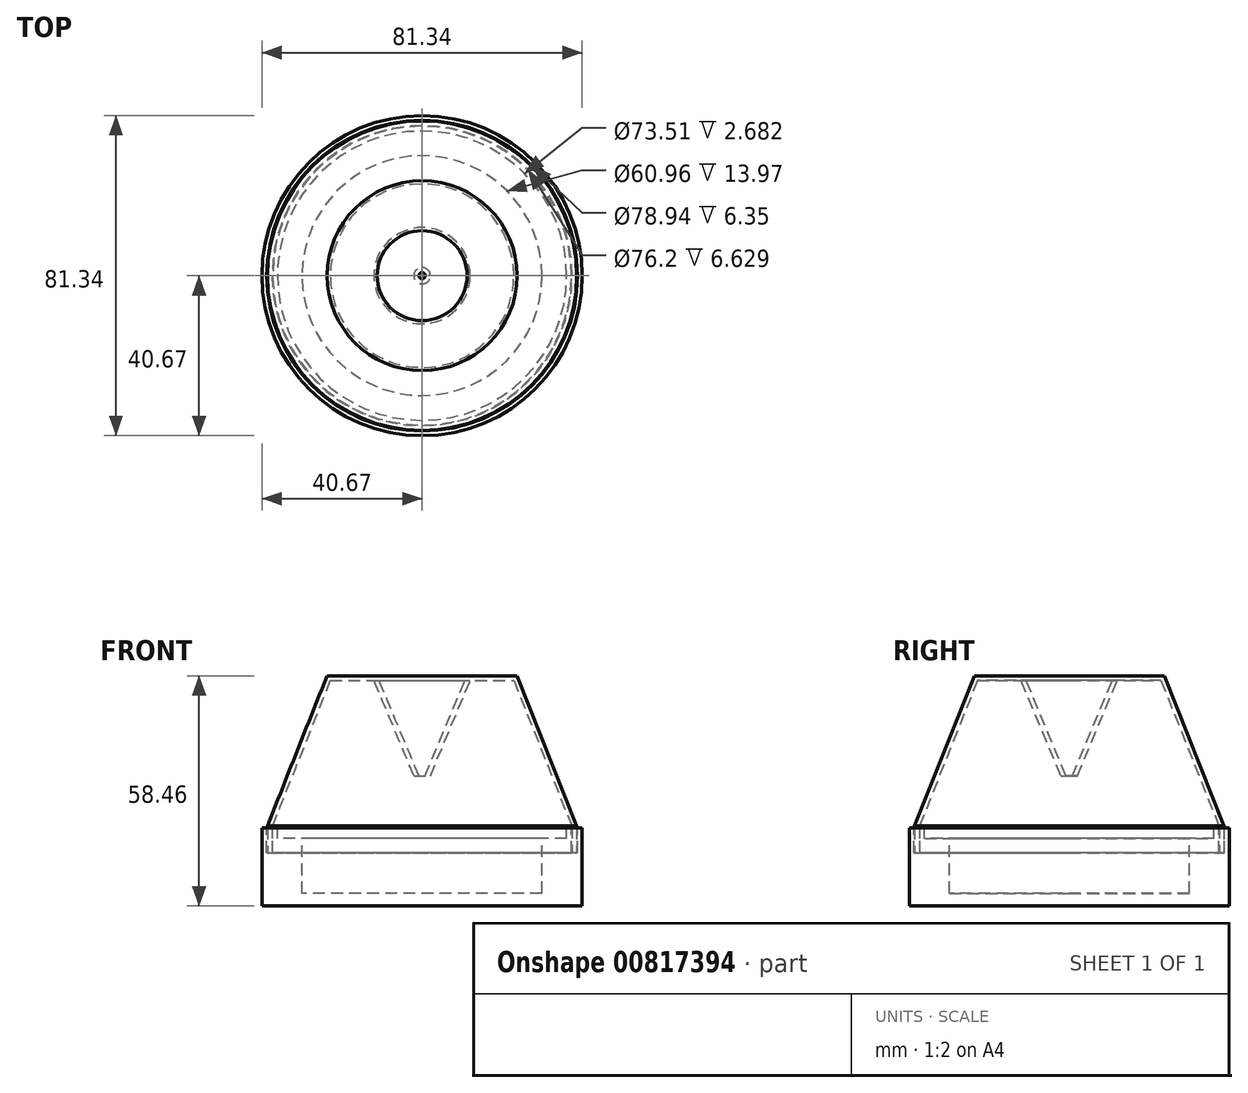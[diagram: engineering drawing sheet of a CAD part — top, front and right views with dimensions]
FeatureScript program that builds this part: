
annotation { "Feature Type Name" : "Feature", "Feature Type Description" : "" }
export const myFeature = defineFeature(function(context is Context, id is Id, definition is map)
    precondition{}
    {
        {
            var Q0;
            Q0=qCreatedBy(makeId("Front.planeOp"),FACE);
            var sketch = newSketch(context, id + "F0", { "sketchPlane" : qUnion([Q0])});
            skLineSegment(sketch, "E0", {"start": v(39.3, 0) * mm, "end": v(24.13, 38.1) * mm});
            skLineSegment(sketch, "E1", {"start": v(24.13, 38.1) * mm, "end": v(11.43, 38.1) * mm});
            skLineSegment(sketch, "E2", {"start": v(11.43, 38.1) * mm, "end": v(0.8, 12.7) * mm});
            skLineSegment(sketch, "E3", {"start": v(39.3, 0) * mm, "end": v(39.3, -6.86) * mm});
            skLineSegment(sketch, "E4.0", {"start": v(12.22, 36.9) * mm, "end": v(2.09, 12.7) * mm});
            skLineSegment(sketch, "E4.1", {"start": v(23.32, 36.9) * mm, "end": v(12.22, 36.9) * mm});
            skLineSegment(sketch, "E4.2", {"start": v(38.1, -0.23) * mm, "end": v(23.32, 36.9) * mm});
            skLineSegment(sketch, "E4.3", {"start": v(38.1, -0.23) * mm, "end": v(38.1, -6.86) * mm});
            skLineSegment(sketch, "E5", {"start": v(38.1, -6.86) * mm, "end": v(39.3, -6.86) * mm});
            skLineSegment(sketch, "E6", {"start": v(0.8, 12.7) * mm, "end": v(2.09, 12.7) * mm});
            skSolve(sketch);
        }
        {
            var Q0;
            Q0=qCreatedBy(makeId("Front.planeOp"),FACE);
            var sketch = newSketch(context, id + "F1", { "sketchPlane" : qUnion([Q0])});
            skLineSegment(sketch, "E7", {"start": v(0, 0) * mm, "end": v(0, 61.65) * mm});
            skSolve(sketch);
        }
        {
            var Q0;
            Q0=makeQuery(id+"F0.imprint","IMPRINT",FACE,{"disambiguationData":[TD([[makeQuery(id+"F0.imprint","IMPRINT",EDGE,{"derivedFrom":sQuery(id+"F0.wireOp",EDGE,"E0")}),1.0]])]});
            var Q1;
            Q1=sQuery(id+"F1.wireOp",EDGE,"E7");
            revolve(context, id + "F2", {"surfaceOperationType" : NewSurfaceOperationType.NEW, "entities" : qUnion([Q0]), "axis" : qUnion([Q1]), "revolveType" : RevolveType.FULL});
        }
        {
            var Q0;
            Q0=qCreatedBy(makeId("Front.planeOp"),FACE);
            var sketch = newSketch(context, id + "F3", { "sketchPlane" : qUnion([Q0])});
            skLineSegment(sketch, "E8", {"start": v(40.67, -0.5) * mm, "end": v(40.67, -20.36) * mm});
            skLineSegment(sketch, "E9", {"start": v(40.67, -20.36) * mm, "end": v(0, -20.36) * mm});
            skLineSegment(sketch, "E10", {"start": v(0, -20.36) * mm, "end": v(0, -17.16) * mm});
            skLineSegment(sketch, "E11", {"start": v(0, -17.16) * mm, "end": v(30.48, -17.16) * mm});
            skLineSegment(sketch, "E12", {"start": v(36.75, -3.19) * mm, "end": v(36.75, -0.5) * mm});
            skLineSegment(sketch, "E13", {"start": v(36.75, -0.5) * mm, "end": v(37.95, -0.5) * mm});
            skLineSegment(sketch, "E14", {"start": v(37.95, -0.5) * mm, "end": v(37.95, -6.86) * mm});
            skLineSegment(sketch, "E15", {"start": v(37.95, -6.86) * mm, "end": v(39.47, -6.86) * mm});
            skLineSegment(sketch, "E16", {"start": v(39.47, -6.86) * mm, "end": v(39.47, -0.5) * mm});
            skLineSegment(sketch, "E17", {"start": v(39.47, -0.5) * mm, "end": v(40.67, -0.5) * mm});
            skLineSegment(sketch, "E18", {"start": v(36.75, -3.19) * mm, "end": v(30.48, -3.19) * mm});
            skLineSegment(sketch, "E19", {"start": v(30.48, -3.19) * mm, "end": v(30.48, -17.16) * mm});
            skSolve(sketch);
        }
        {
            var Q0;
            Q0=qCreatedBy(makeId("Front.planeOp"),FACE);
            var sketch = newSketch(context, id + "F4", { "sketchPlane" : qUnion([Q0])});
            skLineSegment(sketch, "E20", {"start": v(0, 0) * mm, "end": v(0, -13.97) * mm});
            skSolve(sketch);
        }
        {
            var Q0;
            Q0 = qSketchRegion(id + "F3", true);
            var Q1;
            Q1=sQuery(id+"F4.wireOp",EDGE,"E20");
            revolve(context, id + "F5", {"surfaceOperationType" : NewSurfaceOperationType.NEW, "entities" : qUnion([Q0]), "axis" : qUnion([Q1]), "revolveType" : RevolveType.FULL});
        }
    });
